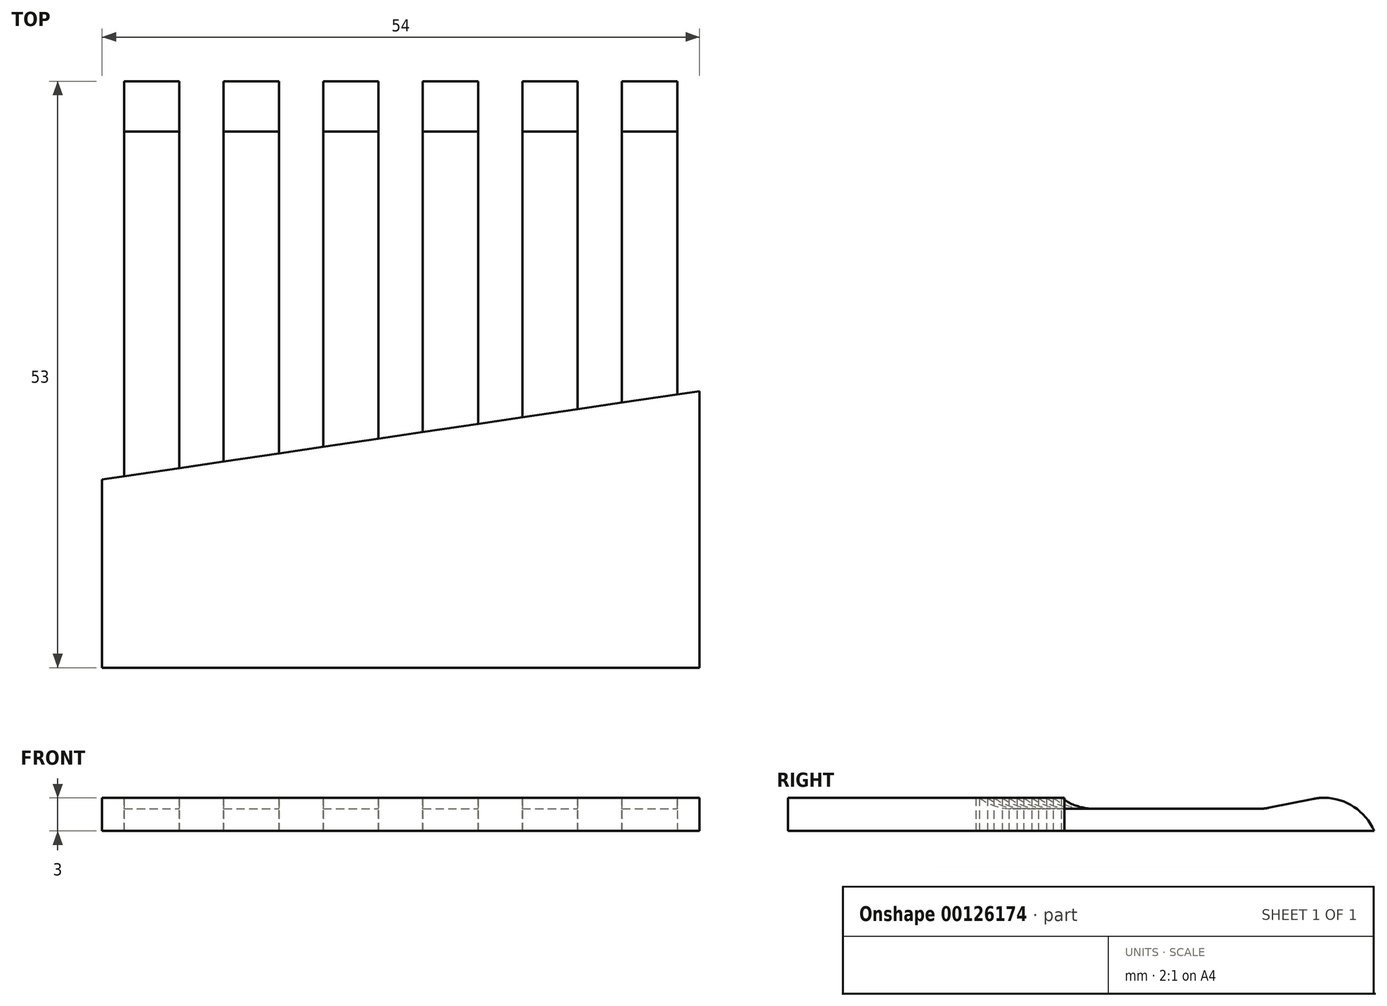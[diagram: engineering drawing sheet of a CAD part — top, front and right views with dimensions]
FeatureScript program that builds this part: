
annotation { "Feature Type Name" : "Feature", "Feature Type Description" : "" }
export const myFeature = defineFeature(function(context is Context, id is Id, definition is map)
    precondition{}
    {
        {
            var Q0;
            Q0=qCreatedBy(makeId("Top.planeOp"),FACE);
            var sketch = newSketch(context, id + "F0", { "sketchPlane" : qUnion([Q0])});
            skLineSegment(sketch, "E0.bottom", {"start": v(-25.72, -18.97) * mm, "end": v(28.28, -18.97) * mm});
            skLineSegment(sketch, "E0.top", {"start": v(-25.72, 34.03) * mm, "end": v(28.28, 34.03) * mm});
            skLineSegment(sketch, "E0.left", {"start": v(-25.72, -18.97) * mm, "end": v(-25.72, 34.03) * mm});
            skLineSegment(sketch, "E0.right", {"start": v(28.28, -18.97) * mm, "end": v(28.28, 34.03) * mm});
            skSolve(sketch);
        }
        {
            var Q0;
            Q0 = qSketchRegion(id + "F0", true);
            extrude(context, id + "F1", {"entities" : qUnion([Q0]), "depth" : 3 * mm});
        }
        {
            var Q0;
            Q0=makeQuery(id+"F1.opExtrude","SWEPT_FACE",FACE,{"disambiguationData":[OSD([sQuery(id+"F0.wireOp",EDGE,"E0.right")])]});
            var sketch = newSketch(context, id + "F2", { "sketchPlane" : qUnion([Q0])});
            skLineSegment(sketch, "E1", {"start": v(-18.97, 3) * mm, "end": v(6.03, 3) * mm, "construction": true});
            skLineSegment(sketch, "E2", {"start": v(6.03, 3) * mm, "end": v(6.03, 2) * mm});
            skLineSegment(sketch, "E3", {"start": v(6.03, 2) * mm, "end": v(24.03, 2) * mm});
            skLineSegment(sketch, "E4", {"start": v(24.03, 2) * mm, "end": v(29.03, 3) * mm});
            skLineSegment(sketch, "E5", {"start": v(6.03, 3) * mm, "end": v(29.03, 3) * mm});
            skSolve(sketch);
        }
        {
            var Q0;
            Q0 = qSketchRegion(id + "F2", true);
            extrude(context, id + "F3", {"entities" : qUnion([Q0]), "operationType" : NewBodyOperationType.REMOVE, "oppositeDirection" : true, "depth" : 54 * mm});
        }
        {
            var Q0;
            Q0=makeQuery(id+"F3.boolean.opBoolean","COPY",EDGE,{"derivedFrom":makeQuery(id+"F3.opExtrude","SWEPT_EDGE",EDGE,{"disambiguationData":[OSD([sQuery(id+"F2.wireOp",EDGE,"E3"),sQuery(id+"F2.wireOp",EDGE,"E4")])]})});
            fillet(context, id + "F4", {"entities" : qUnion([Q0]), "radius" : 5 * mm, "tangentPropagation" : true, "allowEdgeOverflow" : false});
        }
        {
            var Q0;
            Q0=makeQuery(id+"F3.boolean.opBoolean","COPY",EDGE,{"derivedFrom":makeQuery(id+"F3.opExtrude","SWEPT_EDGE",EDGE,{"disambiguationData":[OSD([sQuery(id+"F0.wireOp",EDGE,"E0.right"),sQuery(id+"F2.wireOp",EDGE,"E4"),sQuery(id+"F2.wireOp",EDGE,"E5")])]})});
            fillet(context, id + "F5", {"entities" : qUnion([Q0]), "radius" : 5 * mm, "tangentPropagation" : true, "allowEdgeOverflow" : false});
        }
        {
            var Q0;
            Q0=makeQuery(id+"F1.opExtrude","CAP_EDGE",EDGE,{"disambiguationData":[OSD([sQuery(id+"F0.wireOp",EDGE,"E0.top")])],"isStart":false});
            fillet(context, id + "F6", {"entities" : qUnion([Q0]), "radius" : 5 * mm, "tangentPropagation" : true, "allowEdgeOverflow" : false});
        }
        {
            var Q0;
            {var subQ0=sQuery(id+"F0.wireOp",EDGE,"E0.bottom");var subQ1=sQuery(id+"F0.wireOp",EDGE,"E0.left");var subQ2=sQuery(id+"F0.wireOp",EDGE,"E0.right");Q0=makeQuery(id+"F3.boolean.opBoolean","SPLIT",FACE,{"disambiguationData":[TD([makeQuery(id+"F1.opExtrude","SWEPT_FACE",FACE,{"disambiguationData":[OSD([subQ0])]})])],"derivedFrom":makeQuery(id+"F1.opExtrude","CAP_FACE",FACE,{"disambiguationData":[OSD([subQ0,sQuery(id+"F0.wireOp",EDGE,"E0.top"),subQ1,subQ2])],"isStart":false})});}
            var sketch = newSketch(context, id + "F7", { "sketchPlane" : qUnion([Q0])});
            skLineSegment(sketch, "E6", {"start": v(-25.72, -18.97) * mm, "end": v(-25.72, -1.97) * mm, "construction": true});
            skLineSegment(sketch, "E7", {"start": v(-25.72, -1.97) * mm, "end": v(-25.72, 6.03) * mm});
            skLineSegment(sketch, "E8", {"start": v(-25.72, 6.03) * mm, "end": v(28.28, 6.03) * mm});
            skLineSegment(sketch, "E9", {"start": v(28.28, 6.03) * mm, "end": v(-25.72, -1.97) * mm});
            skSolve(sketch);
        }
        {
            var Q0;
            Q0 = qSketchRegion(id + "F7", true);
            extrude(context, id + "F8", {"entities" : qUnion([Q0]), "operationType" : NewBodyOperationType.REMOVE, "oppositeDirection" : true, "depth" : 1 * mm});
        }
        {
            var Q0;
            Q0=makeQuery(id+"F8.boolean.opBoolean","COPY",EDGE,{"derivedFrom":makeQuery(id+"F8.opExtrude","CAP_EDGE",EDGE,{"disambiguationData":[OSD([sQuery(id+"F7.wireOp",EDGE,"E9")])],"isStart":false})});
            fillet(context, id + "F9", {"entities" : qUnion([Q0]), "radius" : 5 * mm, "tangentPropagation" : true, "allowEdgeOverflow" : false});
        }
        {
            var Q0;
            Q0=makeQuery(id+"F1.opExtrude","CAP_FACE",FACE,{"disambiguationData":[OSD([sQuery(id+"F0.wireOp",EDGE,"E0.bottom"),sQuery(id+"F0.wireOp",EDGE,"E0.top"),sQuery(id+"F0.wireOp",EDGE,"E0.left"),sQuery(id+"F0.wireOp",EDGE,"E0.right")])],"isStart":true});
            var sketch = newSketch(context, id + "F10", { "sketchPlane" : qUnion([Q0])});
            skLineSegment(sketch, "E10", {"start": v(28.28, -6.03) * mm, "end": v(26.28, -5.73) * mm});
            skLineSegment(sketch, "E11", {"start": v(26.28, -5.73) * mm, "end": v(26.28, -34.03) * mm});
            skLineSegment(sketch, "E12", {"start": v(26.28, -34.03) * mm, "end": v(28.28, -34.03) * mm});
            skLineSegment(sketch, "E13", {"start": v(28.28, -34.03) * mm, "end": v(28.28, -6.03) * mm});
            skLineSegment(sketch, "E14", {"start": v(26.28, -34.03) * mm, "end": v(21.28, -34.03) * mm, "construction": true});
            skLineSegment(sketch, "E15", {"start": v(21.28, -34.03) * mm, "end": v(17.28, -34.03) * mm});
            skLineSegment(sketch, "E16", {"start": v(17.28, -34.03) * mm, "end": v(12.28, -34.03) * mm, "construction": true});
            skLineSegment(sketch, "E17", {"start": v(12.28, -34.03) * mm, "end": v(8.28, -34.03) * mm});
            skLineSegment(sketch, "E18", {"start": v(8.28, -34.03) * mm, "end": v(3.28, -34.03) * mm, "construction": true});
            skLineSegment(sketch, "E19", {"start": v(3.28, -34.03) * mm, "end": v(-0.72, -34.03) * mm});
            skLineSegment(sketch, "E20", {"start": v(-0.72, -34.03) * mm, "end": v(-5.72, -34.03) * mm, "construction": true});
            skLineSegment(sketch, "E21", {"start": v(-5.72, -34.03) * mm, "end": v(-9.72, -34.03) * mm});
            skLineSegment(sketch, "E22", {"start": v(-9.72, -34.03) * mm, "end": v(-14.72, -34.03) * mm, "construction": true});
            skLineSegment(sketch, "E23", {"start": v(-14.72, -34.03) * mm, "end": v(-18.72, -34.03) * mm});
            skLineSegment(sketch, "E24", {"start": v(-18.72, -34.03) * mm, "end": v(-23.72, -34.03) * mm, "construction": true});
            skLineSegment(sketch, "E25", {"start": v(-23.72, -34.03) * mm, "end": v(-25.72, -34.03) * mm});
            skLineSegment(sketch, "E26", {"start": v(-25.72, -34.03) * mm, "end": v(-25.72, 1.97) * mm});
            skLineSegment(sketch, "E27", {"start": v(21.28, -4.99) * mm, "end": v(17.28, -4.4) * mm});
            skLineSegment(sketch, "E28", {"start": v(21.28, -34.03) * mm, "end": v(21.28, -4.99) * mm});
            skLineSegment(sketch, "E29", {"start": v(17.28, -34.03) * mm, "end": v(17.28, -4.4) * mm});
            skLineSegment(sketch, "E30", {"start": v(12.28, -34.03) * mm, "end": v(12.28, -3.66) * mm});
            skLineSegment(sketch, "E31", {"start": v(8.28, -34.03) * mm, "end": v(8.28, -3.06) * mm});
            skLineSegment(sketch, "E32", {"start": v(3.28, -34.03) * mm, "end": v(3.28, -2.32) * mm});
            skLineSegment(sketch, "E33", {"start": v(-0.72, -34.03) * mm, "end": v(-0.72, -1.73) * mm});
            skLineSegment(sketch, "E34", {"start": v(-5.72, -34.03) * mm, "end": v(-5.72, -0.99) * mm});
            skLineSegment(sketch, "E35", {"start": v(-9.72, -34.03) * mm, "end": v(-9.72, -0.4) * mm});
            skLineSegment(sketch, "E36", {"start": v(-14.72, -34.03) * mm, "end": v(-14.72, 0.34) * mm});
            skLineSegment(sketch, "E37", {"start": v(-18.72, -34.03) * mm, "end": v(-18.72, 0.94) * mm});
            skLineSegment(sketch, "E38", {"start": v(-23.72, -34.03) * mm, "end": v(-23.72, 1.68) * mm});
            skLineSegment(sketch, "E39.trimOffspring", {"start": v(12.28, -3.66) * mm, "end": v(8.28, -3.06) * mm});
            skLineSegment(sketch, "E40.trimOffspring", {"start": v(3.28, -2.32) * mm, "end": v(-0.72, -1.73) * mm});
            skLineSegment(sketch, "E41.trimOffspring", {"start": v(-5.72, -0.99) * mm, "end": v(-9.72, -0.4) * mm});
            skLineSegment(sketch, "E42.trimOffspring", {"start": v(-14.72, 0.34) * mm, "end": v(-18.72, 0.94) * mm});
            skLineSegment(sketch, "E43.trimOffspring", {"start": v(-23.72, 1.68) * mm, "end": v(-25.72, 1.97) * mm});
            skSolve(sketch);
        }
        {
            var Q0;
            Q0 = qSketchRegion(id + "F10", true);
            extrude(context, id + "F11", {"entities" : qUnion([Q0]), "operationType" : NewBodyOperationType.REMOVE, "endBound" : BoundingType.THROUGH_ALL, "oppositeDirection" : true, "depth" : 25 * mm});
        }
    });
